FCSTD DOCUMENT  (FreeCAD 0.16R6703 (Git))
Label: randompart
License: All rights reserved
LicenseURL: http://en.wikipedia.org/wiki/All_rights_reserved
objects: Sketcher::SketchObject×1
note: 1 computed .brp shape members not serialized (recipe doc carries the construction recipe); baked Part::Feature solids carry a one-line shape summary decoded from their .brp

FEATURE [Sketcher::SketchObject] Sketch
  sketch-geometry (16):
    g0: LineSegment [constr] StartX=0 StartY=0 StartZ=0 EndX=28.5317 EndY=9.27051 EndZ=0
    g1: LineSegment [constr] StartX=0 StartY=0 StartZ=0 EndX=0 EndY=30 EndZ=0
    g2: LineSegment [constr] StartX=0 StartY=0 StartZ=0 EndX=-28.5317 EndY=9.27051 EndZ=0
    g3: LineSegment [constr] StartX=0 StartY=0 StartZ=0 EndX=-17.6336 EndY=-24.2705 EndZ=0
    g4: LineSegment [constr] StartX=0 StartY=0 StartZ=0 EndX=17.6336 EndY=-24.2705 EndZ=0
    g5: Circle CenterX=0 CenterY=0 CenterZ=0 NormalX=0 NormalY=0 NormalZ=1 Radius=10
    g6: ArcOfCircle CenterX=0 CenterY=30 CenterZ=0 NormalX=0 NormalY=0 NormalZ=1 Radius=8 StartAngle=6.03643 EndAngle=9.67153
    g7: ArcOfCircle CenterX=28.5317 CenterY=9.27051 CenterZ=0 NormalX=0 NormalY=0 NormalZ=1 Radius=8 StartAngle=4.7798 EndAngle=8.41489
    g8: ArcOfCircle CenterX=17.6336 CenterY=-24.2705 CenterZ=0 NormalX=0 NormalY=0 NormalZ=1 Radius=8 StartAngle=3.52076 EndAngle=7.15825
    g9: ArcOfCircle CenterX=-17.6336 CenterY=-24.2705 CenterZ=0 NormalX=0 NormalY=0 NormalZ=1 Radius=8 StartAngle=2.26653 EndAngle=5.97087
    g10: ArcOfCircle CenterX=-28.5317 CenterY=9.27051 CenterZ=0 NormalX=0 NormalY=0 NormalZ=1 Radius=8 StartAngle=1.00989 EndAngle=4.64498
    g11: ArcOfCircle CenterX=-18.4245 CenterY=25.3592 CenterZ=0 NormalX=0 NormalY=0 NormalZ=1 Radius=11 StartAngle=4.15148 EndAngle=6.52994
    g12: ArcOfCircle CenterX=-29.8115 CenterY=-9.68634 CenterZ=0 NormalX=0 NormalY=0 NormalZ=1 Radius=11 StartAngle=5.40811 EndAngle=7.78658
    g13: ArcOfCircle CenterX=-0.0169428 CenterY=-31.3033 CenterZ=0 NormalX=0 NormalY=0 NormalZ=1 Radius=11 StartAngle=0.379166 EndAngle=2.71268
    g14: ArcOfCircle CenterX=29.8115 CenterY=-9.68634 CenterZ=0 NormalX=0 NormalY=0 NormalZ=1 Radius=11 StartAngle=1.63821 EndAngle=4.01666
    g15: ArcOfCircle CenterX=18.4245 CenterY=25.3592 CenterZ=0 NormalX=0 NormalY=0 NormalZ=1 Radius=11 StartAngle=2.89484 EndAngle=5.2733
  constraints (54):
    c: PointOnObject(g1,g-2)
    c: Vertical(g1)
    c: Coincident(g3,g-1)
    c: Coincident(g4,g-1)
    c: Coincident(g5,g-1)
    c: Coincident(g6,g1)
    c: Coincident(g7,g0)
    c: Coincident(g8,g4)
    c: Coincident(g9,g3)
    c: Coincident(g11,g6)
    c: Coincident(g11,g10)
    c: Coincident(g12,g10)
    c: Coincident(g12,g9)
    c: Coincident(g13,g9)
    c: Coincident(g14,g8)
    c: Coincident(g14,g7)
    c: Coincident(g15,g7)
    c: Coincident(g15,g6)
    c: Equal(g0,g1)
    c: Equal(g1,g2)
    c: Equal(g2,g3)
    c: Equal(g3,g4)
    c: Equal(g6,g7)
    c: Equal(g7,g8)
    c: Equal(g8,g9)
    c: Equal(g9,g10)
    c: Tangent(g13,g8) = 1.5708
    c: Coincident(g2,g-1)
    c: Angle(g0,g1) = 1.25664
    c: Angle(g4,g0) = 1.25664
    c: Angle(g3,g4) = 1.25664
    c: Angle(g2,g3) = 1.25664
    c: Coincident(g2,g10)
    c: Coincident(g0,g-1)
    c: Coincident(g1,g-1)
    c: DistanceY(g-1,g1) = 30
    c: Radius(g10) = 8
    c: Tangent(g9,g9) = -1.5708
    c: Tangent(g8,g8) = -1.5708
    c: Tangent(g8,g8) = -1.5708
    c: Tangent(g14,g8)
    c: Tangent(g14,g7)
    c: Tangent(g15,g7)
    c: Tangent(g6,g15)
    c: Tangent(g11,g6)
    c: Tangent(g11,g10)
    c: Tangent(g10,g12)
    c: Tangent(g12,g9)
    c: Radius(g5) = 10
    c: Radius(g12) = 11
    c: Equal(g11,g15)
    c: Equal(g15,g14)
    c: Equal(g14,g13)
    c: Equal(g13,g12)
